# Revit family: Spannbügel, zn
name_source: partatom
category: HLS-Bauteile
revit_build: Autodesk Revit 2017 (Build: 20190507_1515(x64)
units: mm (PartAtom-declared; Revit-internal decimal feet)

## family parameters
Arbeitsebenenbasiert = Ja
Beim Laden mit Abzugskörper schneiden = Nein
Bemaßung runder Anschluss = Durchmesser verwenden
Gemeinsam genutzt = Ja
Immer vertikal = Nein
Raumberechnungspunkt = Nein
Teiletyp = Normal

## types (2) — shared parameters
Achsabstand U-Bügel = 56 mm
B1 = 56 mm  [stored 0.183727 ft]
Breite Spannwinkel = 80 mm
Fabrikat = MEFA
Flachscheibe = Unterlegscheibe : Unterlegscheibe 10.5x20x2
Klemmdicke = 26 mm
Kurztext1 = Spannbügel M10 45
Material = Stahl
Mutter = Sechskantmutter : Sechskantmutter M10
Profiltyp = 45
S = 6 mm  [stored 0.019685 ft]
Spanwinkel = Spannwinkel : Spanwinkel 80/20/6
Vorgabe-Ansicht = 1219 mm
max. zul. Last Fx = 0.00 kN
max. zul. Last Fy = 0.00 kN
max. zul. Last Fz = 0.00 kN
min. Randabstand = 70 mm  [stored 0.229659 ft]

## per-type parameters (varying)
| type | Artikelnummer | EAN | Gewicht | Gewicht pro Bauteil | Kurztext2 | L | Länge U-Bügel | Rundstahl |
| Spannbügel M10 45- 60, zn | 0816720/zn | 4250928456397 | 0.40 kg | 0.40 kg | Profilhöhe 26 - 60 Klemmdicke 26 mm ZnNi | 80 mm  [stored 0.262467 ft] | 100 mm | Rundstahl U-Bügel : Rundstahl U Bügel 56-100 M10 |
| Spannbügel M10 45- 90, zn | 0816730/zn | 4250928456380 | 0.44 kg | 0.44 kg | Profilhöhe 75 + 90 Klemmdicke 26 mm ZnNi | 110 mm  [stored 0.360892 ft] | 140 mm | Rundstahl U-Bügel : Rundstahl U Bügel 56-140 M10 |

note: [stored X ft] marks values corroborated as IEEE doubles in the binary element streams (Revit-internal decimal feet)

## geometry (parser evidence)
native form markers: Sweep x1
no freeform markers — native parametric forms only
